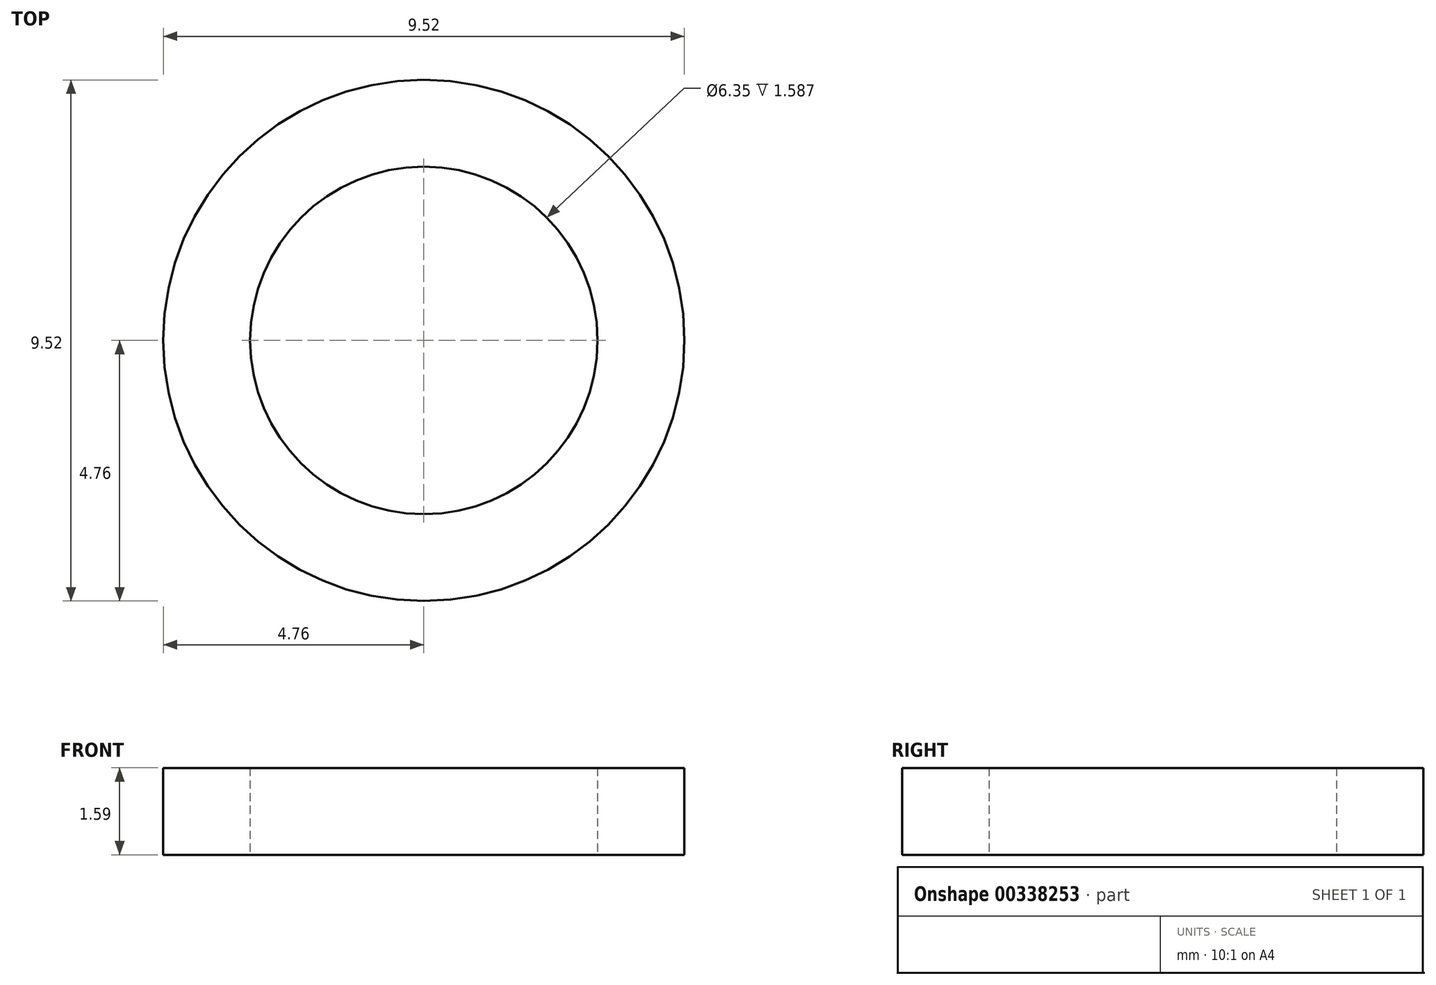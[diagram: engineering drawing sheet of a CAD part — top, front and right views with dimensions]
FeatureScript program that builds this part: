
annotation { "Feature Type Name" : "Feature", "Feature Type Description" : "" }
export const myFeature = defineFeature(function(context is Context, id is Id, definition is map)
    precondition{}
    {
        {
            var Q0;
            Q0=qCreatedBy(makeId("Top.planeOp"),FACE);
            var sketch = newSketch(context, id + "F0", { "sketchPlane" : qUnion([Q0])});
            skCircle(sketch, "E0", {"center": v(0, 0) * mm, "radius": 3.18 * mm});
            skCircle(sketch, "E1", {"center": v(0, 0) * mm, "radius": 4.76 * mm});
            skSolve(sketch);
        }
        {
            var Q0;
            Q0 = qSketchRegion(id + "F0", true);
            extrude(context, id + "F1", {"entities" : qUnion([Q0]), "depth" : 1.59 * mm});
        }
    });
